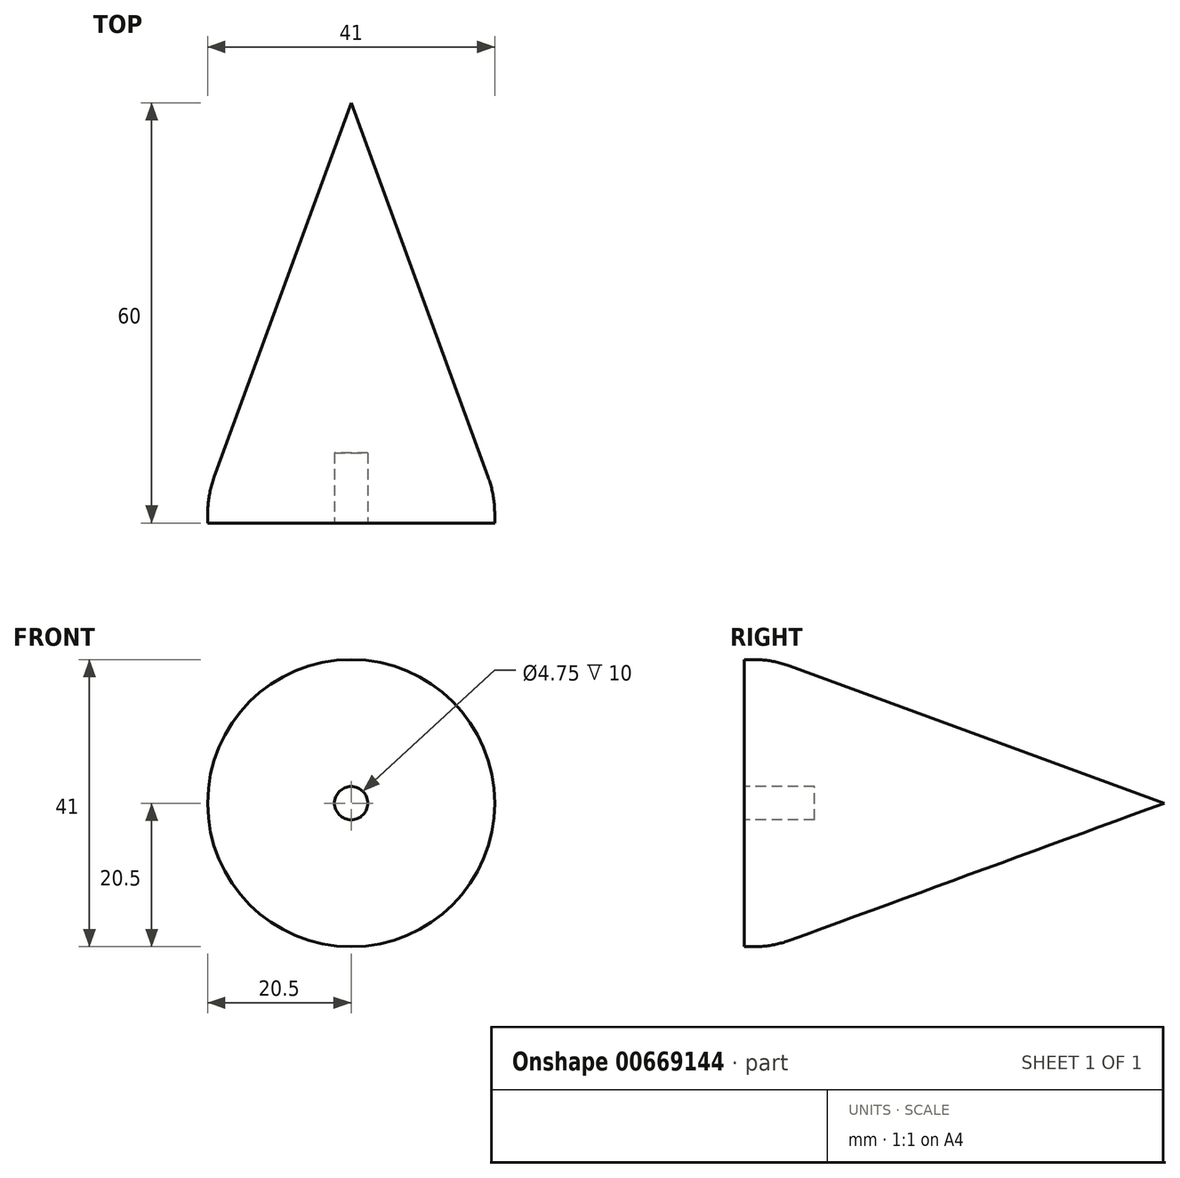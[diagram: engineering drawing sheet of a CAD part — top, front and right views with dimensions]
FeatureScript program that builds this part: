
annotation { "Feature Type Name" : "Feature", "Feature Type Description" : "" }
export const myFeature = defineFeature(function(context is Context, id is Id, definition is map)
    precondition{}
    {
        {
            var Q0;
            Q0=qCreatedBy(makeId("Right.planeOp"),FACE);
            var sketch = newSketch(context, id + "F0", { "sketchPlane" : qUnion([Q0])});
            skLineSegment(sketch, "E0", {"start": v(0, 0) * mm, "end": v(0, 20.5) * mm});
            skLineSegment(sketch, "E1", {"start": v(0, 20.5) * mm, "end": v(1.34, 20.5) * mm});
            skLineSegment(sketch, "E2", {"start": v(6.5, 19.59) * mm, "end": v(60, 0) * mm});
            skLineSegment(sketch, "E3", {"start": v(60, 0) * mm, "end": v(0, 0) * mm});
            skPoint(sketch, "E4.visualSharp", {"position": v(4, 20.5) * mm});
            skArc(sketch, "E4.filletArc", {"start": v(6.5, 19.59) * mm, "mid": v(3.96, 20.27) * mm, "end": v(1.34, 20.5) * mm});
            skSolve(sketch);
        }
        {
            var Q0;
            Q0 = qSketchRegion(id + "F0", true);
            var Q1;
            Q1=sQuery(id+"F0.wireOp",EDGE,"E3");
            revolve(context, id + "F1", {"entities" : qUnion([Q0]), "axis" : qUnion([Q1]), "revolveType" : RevolveType.FULL});
        }
        {
            var Q0;
            Q0=qCreatedBy(makeId("Front.planeOp"),FACE);
            var sketch = newSketch(context, id + "F2", { "sketchPlane" : qUnion([Q0])});
            skCircle(sketch, "E5", {"center": v(0, 0) * mm, "radius": 2.38 * mm});
            skSolve(sketch);
        }
        {
            var Q0;
            Q0 = qSketchRegion(id + "F2", true);
            extrude(context, id + "F3", {"entities" : qUnion([Q0]), "operationType" : NewBodyOperationType.REMOVE, "oppositeDirection" : true, "depth" : 10 * mm, "offsetDistance" : 25 * mm});
        }
    });
